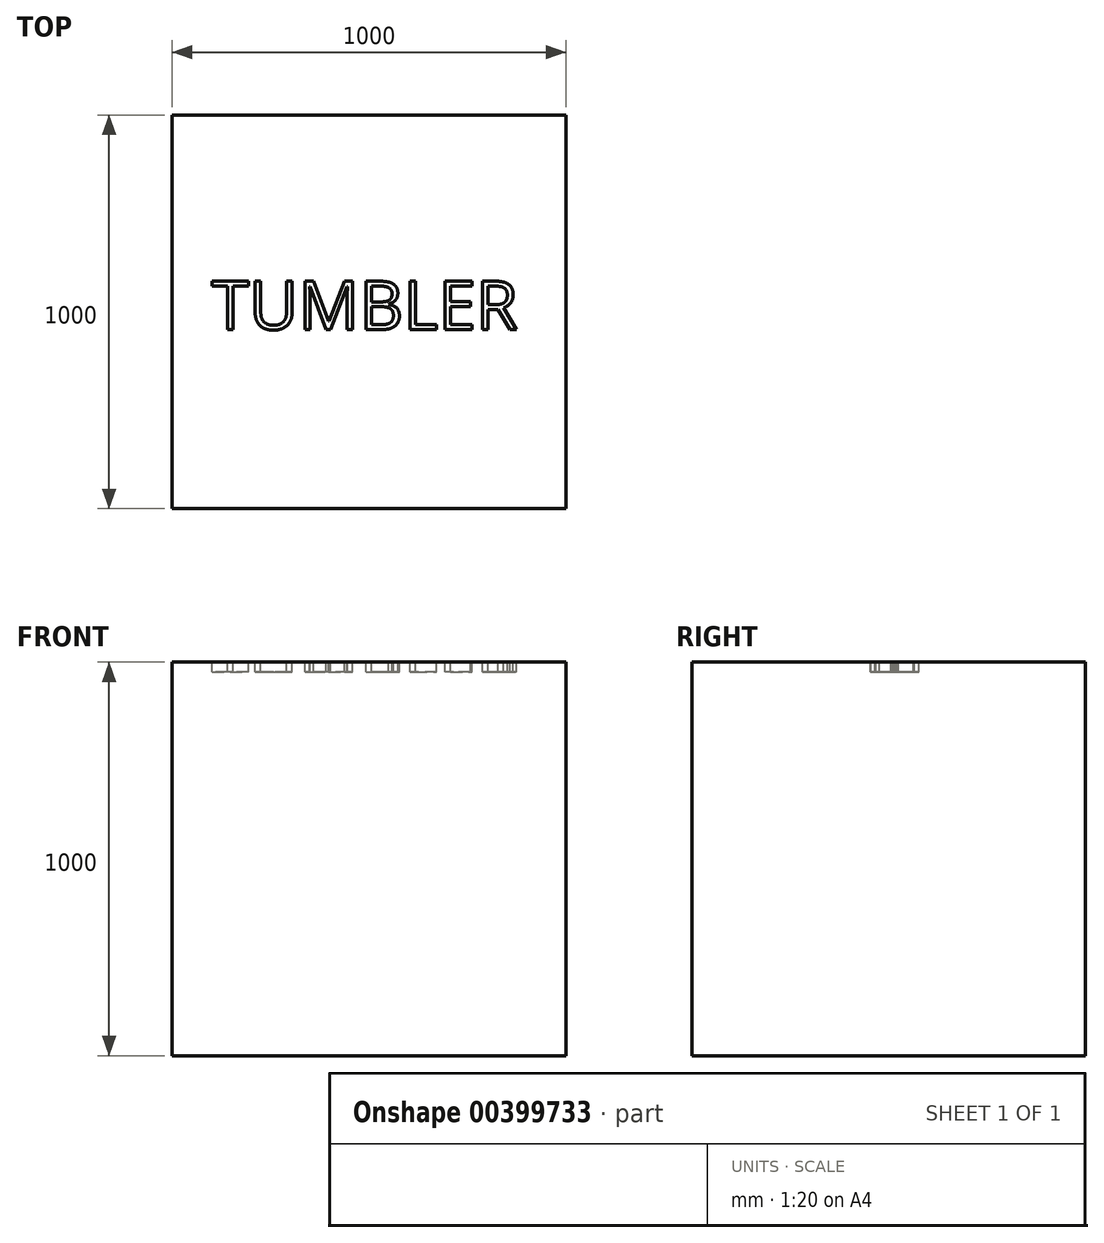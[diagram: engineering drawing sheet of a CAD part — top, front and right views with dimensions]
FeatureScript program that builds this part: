
annotation { "Feature Type Name" : "Feature", "Feature Type Description" : "" }
export const myFeature = defineFeature(function(context is Context, id is Id, definition is map)
    precondition{}
    {
        {
            var Q0;
            Q0=qCreatedBy(makeId("Top.planeOp"),FACE);
            var sketch = newSketch(context, id + "F0", { "sketchPlane" : qUnion([Q0])});
            skLineSegment(sketch, "E0.bottom", {"start": v(500, -500) * mm, "end": v(-500, -500) * mm});
            skLineSegment(sketch, "E0.top", {"start": v(500, 500) * mm, "end": v(-500, 500) * mm});
            skLineSegment(sketch, "E0.left", {"start": v(500, -500) * mm, "end": v(500, 500) * mm});
            skLineSegment(sketch, "E0.right", {"start": v(-500, -500) * mm, "end": v(-500, 500) * mm});
            skPoint(sketch, "E0.middle", {"position": v(0, 0) * mm});
            skSolve(sketch);
        }
        {
            var Q0;
            Q0 = qSketchRegion(id + "F0", true);
            extrude(context, id + "F1", {"entities" : qUnion([Q0]), "depth" : 1000 * mm});
        }
        {
            var Q0;
            Q0=makeQuery(id+"F1.opExtrude","CAP_FACE",FACE,{"disambiguationData":[OSD([sQuery(id+"F0.wireOp",EDGE,"E0.bottom"),sQuery(id+"F0.wireOp",EDGE,"E0.top"),sQuery(id+"F0.wireOp",EDGE,"E0.left"),sQuery(id+"F0.wireOp",EDGE,"E0.right")])],"isStart":false});
            var sketch = newSketch(context, id + "F2", { "sketchPlane" : qUnion([Q0])});
            skText(sketch, "E1", { "text": "TUMBLER\n", "fontName": "OpenSans-Regular.ttf"});
            const initialGuessF2  = {"E1": [-0.4, -0.04506, 1, 0, 0.12376]};
            skSetInitialGuess(sketch, initialGuessF2);
            skSolve(sketch);
        }
        {
            var Q0;
            Q0 = qSketchRegion(id + "F2", true);
            extrude(context, id + "F3", {"entities" : qUnion([Q0]), "operationType" : NewBodyOperationType.REMOVE, "oppositeDirection" : true, "depth" : 25 * mm});
        }
    });
